# Revit family: Overhead_Door-CHI-Skyline_Flush-LP
name_source: partatom
category: Specialty Equipment
units: mm (PartAtom-declared; Revit-internal decimal feet)

## family parameters
Always vertical = Yes
Cut with Voids When Loaded = No
Host = Wall
OmniClass Number = 23.30.10.21
OmniClass Title = Special Function Doors
Part Type = Normal
Room Calculation Point = No
Round Connector Dimension = Use Diameter
Shared = No

## types (57) — shared parameters
Assembly Code = B2050.10
C Door Bottom Offset = 0.03'
C OFG = 0.00'
C Panel Size = 2
C Side Rail Radius = 1.25'
Certified Windload = Yes
Construction Type = Glass garage doors
Default Elevation = 0.00'
Description = Skyline Garage Doors
Fire Rating = Contact Manufacturer for More Information
Glass Finish = Glass - C.H.I Overhead Doors - Frosted
Impact = Yes
Keynote = 08 30 00
Load Classification = Other
Long Panel = Yes
Manufacturer = C.H.I. Overhead Doors
Manufacturer Fax Number = 800-738-5006
Material Disclaimer = Accents Woodtones, when ordered, contain non-repeating patterns. Color discrepancies may appear differently on desktop displays. Contact Manufacturer for Availability of Finishes per Model
Number of Phases = 1
Number of Poles = 1
Product Documentation Link = https://www.chiohd.com
Product Page URL = https://www.chiohd.com
Short Panel = No
Thickness = 0.17'
URL = https://www.chiohd.com
Version = 2021-v1.a
Voltage = 115 V

## per-type parameters (varying)
| type | Air Infiltration | C Model | DASMA Thermal Verification Program | Flame Spread | IECC Compliant | Model | Panel Finish | R-Value | Steel Gauge | U Factor |
| 2147 - Almond | Contact Manufacturer for More Information | 5 | No | Contact Manufacturer for More Information | No | 2147 | Metal - Powder Coat - C.H.I Overhead Doors - Almond | 10.29 | 27 | 0.29 |
| 2147 - Black | Contact Manufacturer for More Information | 5 | No | Contact Manufacturer for More Information | No | 2147 | Metal - Powder Coat - C.H.I Overhead Doors - Black | 10.29 | 27 | 0.29 |
| 2147 - Brown | Contact Manufacturer for More Information | 5 | No | Contact Manufacturer for More Information | No | 2147 | Metal - Powder Coat - C.H.I Overhead Doors - Brown | 10.29 | 27 | 0.29 |
| 2147 - Graphite | Contact Manufacturer for More Information | 5 | No | Contact Manufacturer for More Information | No | 2147 | Metal - Powder Coat - C.H.I Overhead Doors - Graphite | 10.29 | 27 | 0.29 |
| 2147 - Gray | Contact Manufacturer for More Information | 5 | No | Contact Manufacturer for More Information | No | 2147 | Metal - Powder Coat - C.H.I Overhead Doors - Gray | 10.29 | 27 | 0.29 |
| 2147 - Sandstone | Contact Manufacturer for More Information | 5 | No | Contact Manufacturer for More Information | No | 2147 | Metal - Powder Coat - C.H.I Overhead Doors - Sandstone | 10.29 | 27 | 0.29 |
| 2147 - White | Contact Manufacturer for More Information | 5 | No | Contact Manufacturer for More Information | No | 2147 | Metal - Powder Coat - C.H.I Overhead Doors - White | 10.29 | 27 | 0.29 |
| 2147 - Carbon Oak | Contact Manufacturer for More Information | 5 | No | Contact Manufacturer for More Information | No | 2147 | Wood - Accents Woodtones - C.H.I Overhead Doors - Skyline Flush - Carbon Oak | 10.29 | 27 | 0.29 |
| 2147 - Cedar | Contact Manufacturer for More Information | 5 | No | Contact Manufacturer for More Information | No | 2147 | Wood - Accents Woodtones - C.H.I Overhead Doors - Skyline Flush - Cedar | 10.29 | 27 | 0.29 |
| 2147 - Dark Oak | Contact Manufacturer for More Information | 5 | No | Contact Manufacturer for More Information | No | 2147 | Wood - Accents Woodtones - C.H.I Overhead Doors - Skyline Flush - Dark Oak | 10.29 | 27 | 0.29 |
| 2147 - Driftwood | Contact Manufacturer for More Information | 5 | No | Contact Manufacturer for More Information | No | 2147 | Wood - Accents Woodtones - C.H.I Overhead Doors - Skyline Flush - Driftwood | 10.29 | 27 | 0.29 |
| 2147 - Mahogany | Contact Manufacturer for More Information | 5 | No | Contact Manufacturer for More Information | No | 2147 | Wood - Accents Woodtones - C.H.I Overhead Doors - Skyline Flush - Mahogany | 10.29 | 27 | 0.29 |
| 2147 - Natural Oak | Contact Manufacturer for More Information | 5 | No | Contact Manufacturer for More Information | No | 2147 | Wood - Accents Woodtones - C.H.I Overhead Doors - Skyline Flush - Natural Oak | 10.29 | 27 | 0.29 |
| 2147 - Walnut | Contact Manufacturer for More Information | 5 | No | Contact Manufacturer for More Information | No | 2147 | Wood - Accents Woodtones - C.H.I Overhead Doors - Skyline Flush - Walnut | 10.29 | 27 | 0.29 |
| 2148 - Almond | 0.1 | 6 | Yes | 15 | Yes | 2148 | Metal - Powder Coat - C.H.I Overhead Doors - Almond | 17.54 | 27 | 0.19 |
| 2148 - Black | 0.1 | 6 | Yes | 15 | Yes | 2148 | Metal - Powder Coat - C.H.I Overhead Doors - Black | 17.54 | 27 | 0.19 |
| 2148 - Bronze | 0.1 | 6 | Yes | 15 | Yes | 2148 | Metal - Powder Coat - C.H.I Overhead Doors - Bronze | 17.54 | 27 | 0.19 |
| 2148 - Brown | 0.1 | 6 | Yes | 15 | Yes | 2148 | Metal - Powder Coat - C.H.I Overhead Doors - Brown | 17.54 | 27 | 0.19 |
| 2148 - Desert Tan | 0.1 | 6 | Yes | 15 | Yes | 2148 | Metal - Powder Coat - C.H.I Overhead Doors - Desert Tan | 17.54 | 27 | 0.19 |
| 2148 - Graphite | 0.1 | 6 | Yes | 15 | Yes | 2148 | Metal - Powder Coat - C.H.I Overhead Doors - Graphite | 17.54 | 27 | 0.19 |
| 2148 - Gray | 0.1 | 6 | Yes | 15 | Yes | 2148 | Metal - Powder Coat - C.H.I Overhead Doors - Gray | 17.54 | 27 | 0.19 |
| 2148 - Sandstone | 0.1 | 6 | Yes | 15 | Yes | 2148 | Metal - Powder Coat - C.H.I Overhead Doors - Sandstone | 17.54 | 27 | 0.19 |
| 2148 - White | 0.1 | 6 | Yes | 15 | Yes | 2148 | Metal - Powder Coat - C.H.I Overhead Doors - White | 17.54 | 27 | 0.19 |
| 2148 - Cedar | 0.1 | 6 | Yes | 15 | Yes | 2148 | Wood - Accents Woodtones - C.H.I Overhead Doors - Skyline Flush - Cedar | 17.54 | 27 | 0.19 |
| 2148 - Dark Oak | 0.1 | 6 | Yes | 15 | Yes | 2148 | Wood - Accents Woodtones - C.H.I Overhead Doors - Skyline Flush - Dark Oak | 17.54 | 27 | 0.19 |
| 2148 - Driftwood | 0.1 | 6 | Yes | 15 | Yes | 2148 | Wood - Accents Woodtones - C.H.I Overhead Doors - Skyline Flush - Driftwood | 17.54 | 27 | 0.19 |
| 2148 - Mahogany | 0.1 | 6 | Yes | 15 | Yes | 2148 | Wood - Accents Woodtones - C.H.I Overhead Doors - Skyline Flush - Mahogany | 17.54 | 27 | 0.19 |
| 2148 - Natural Oak | 0.1 | 6 | Yes | 15 | Yes | 2148 | Wood - Accents Woodtones - C.H.I Overhead Doors - Skyline Flush - Natural Oak | 17.54 | 27 | 0.19 |
| 2148 - Walnut | 0.1 | 6 | Yes | 15 | Yes | 2148 | Wood - Accents Woodtones - C.H.I Overhead Doors - Skyline Flush - Walnut | 17.54 | 27 | 0.19 |
| 4140 - Almond | Contact Manufacturer for More Information | 11 | No | Contact Manufacturer for More Information | No | 4140 | Metal - Powder Coat - C.H.I Overhead Doors - Almond | Contact Manufacturer for More Information | 24 | Contact Manufacturer for More Information |
| 4140 - Brown | Contact Manufacturer for More Information | 11 | No | Contact Manufacturer for More Information | No | 4140 | Metal - Powder Coat - C.H.I Overhead Doors - Brown | Contact Manufacturer for More Information | 24 | Contact Manufacturer for More Information |
| 4140 - Sandstone | Contact Manufacturer for More Information | 11 | No | Contact Manufacturer for More Information | No | 4140 | Metal - Powder Coat - C.H.I Overhead Doors - Sandstone | Contact Manufacturer for More Information | 24 | Contact Manufacturer for More Information |
| 4140 - White | Contact Manufacturer for More Information | 11 | No | Contact Manufacturer for More Information | No | 4140 | Metal - Powder Coat - C.H.I Overhead Doors - White | Contact Manufacturer for More Information | 24 | Contact Manufacturer for More Information |
| 4141 - Almond | Contact Manufacturer for More Information | 12 | No | Contact Manufacturer for More Information | No | 4141 | Metal - Powder Coat - C.H.I Overhead Doors - Almond | 7.94 | 24 | Contact Manufacturer for More Information |
| 4141 - Brown | Contact Manufacturer for More Information | 12 | No | Contact Manufacturer for More Information | No | 4141 | Metal - Powder Coat - C.H.I Overhead Doors - Brown | 7.94 | 24 | Contact Manufacturer for More Information |
| 4141 - Sandstone | Contact Manufacturer for More Information | 12 | No | Contact Manufacturer for More Information | No | 4141 | Metal - Powder Coat - C.H.I Overhead Doors - Sandstone | 7.94 | 24 | Contact Manufacturer for More Information |
| 4141 - White | Contact Manufacturer for More Information | 12 | No | Contact Manufacturer for More Information | No | 4141 | Metal - Powder Coat - C.H.I Overhead Doors - White | 7.94 | 24 | Contact Manufacturer for More Information |
| 4150 - Almond | Contact Manufacturer for More Information | 13 | No | Contact Manufacturer for More Information | No | 4150 | Metal - Powder Coat - C.H.I Overhead Doors - Almond | Contact Manufacturer for More Information | 25 | Contact Manufacturer for More Information |
| 4150 - Black | Contact Manufacturer for More Information | 13 | No | Contact Manufacturer for More Information | No | 4150 | Metal - Powder Coat - C.H.I Overhead Doors - Black | Contact Manufacturer for More Information | 25 | Contact Manufacturer for More Information |
| 4150 - Bronze | Contact Manufacturer for More Information | 13 | No | Contact Manufacturer for More Information | No | 4150 | Metal - Powder Coat - C.H.I Overhead Doors - Bronze | Contact Manufacturer for More Information | 25 | Contact Manufacturer for More Information |
| 4150 - Brown | Contact Manufacturer for More Information | 13 | No | Contact Manufacturer for More Information | No | 4150 | Metal - Powder Coat - C.H.I Overhead Doors - Brown | Contact Manufacturer for More Information | 25 | Contact Manufacturer for More Information |
| 4150 - Desert Tan | Contact Manufacturer for More Information | 13 | No | Contact Manufacturer for More Information | No | 4150 | Metal - Powder Coat - C.H.I Overhead Doors - Desert Tan | Contact Manufacturer for More Information | 25 | Contact Manufacturer for More Information |
| 4150 - Gray | Contact Manufacturer for More Information | 13 | No | Contact Manufacturer for More Information | No | 4150 | Metal - Powder Coat - C.H.I Overhead Doors - Gray | Contact Manufacturer for More Information | 25 | Contact Manufacturer for More Information |
| 4150 - Sandstone | Contact Manufacturer for More Information | 13 | No | Contact Manufacturer for More Information | No | 4150 | Metal - Powder Coat - C.H.I Overhead Doors - Sandstone | Contact Manufacturer for More Information | 25 | Contact Manufacturer for More Information |
| 4150 - White | Contact Manufacturer for More Information | 13 | No | Contact Manufacturer for More Information | No | 4150 | Metal - Powder Coat - C.H.I Overhead Doors - White | Contact Manufacturer for More Information | 25 | Contact Manufacturer for More Information |
| 4150 - Classic Woodgrain | Contact Manufacturer for More Information | 13 | No | Contact Manufacturer for More Information | No | 4150 | Wood - Painted Woodtones - C.H.I Overhead Doors - Classic Woodgrain | Contact Manufacturer for More Information | 25 | Contact Manufacturer for More Information |
| 4150 - Modern Woodgrain | Contact Manufacturer for More Information | 13 | No | Contact Manufacturer for More Information | No | 4150 | Wood - Painted Woodtones - C.H.I Overhead Doors - Modern Woodgrain | Contact Manufacturer for More Information | 25 | Contact Manufacturer for More Information |
| 4151 - Almond | Contact Manufacturer for More Information | 14 | No | Contact Manufacturer for More Information | No | 4151 | Metal - Powder Coat - C.H.I Overhead Doors - Almond | 7.94 | 25 | Contact Manufacturer for More Information |
| 4151 - Black | Contact Manufacturer for More Information | 14 | No | Contact Manufacturer for More Information | No | 4151 | Metal - Powder Coat - C.H.I Overhead Doors - Black | 7.94 | 25 | Contact Manufacturer for More Information |
| 4151 - Bronze | Contact Manufacturer for More Information | 14 | No | Contact Manufacturer for More Information | No | 4151 | Metal - Powder Coat - C.H.I Overhead Doors - Bronze | 7.94 | 25 | Contact Manufacturer for More Information |
| 4151 - Brown | Contact Manufacturer for More Information | 14 | No | Contact Manufacturer for More Information | No | 4151 | Metal - Powder Coat - C.H.I Overhead Doors - Brown | 7.94 | 25 | Contact Manufacturer for More Information |
| 4151 - Desert Tan | Contact Manufacturer for More Information | 14 | No | Contact Manufacturer for More Information | No | 4151 | Metal - Powder Coat - C.H.I Overhead Doors - Desert Tan | 7.94 | 25 | Contact Manufacturer for More Information |
| 4151 - Gray | Contact Manufacturer for More Information | 14 | No | Contact Manufacturer for More Information | No | 4151 | Metal - Powder Coat - C.H.I Overhead Doors - Gray | 7.94 | 25 | Contact Manufacturer for More Information |
| 4151 - Sandstone | Contact Manufacturer for More Information | 14 | No | Contact Manufacturer for More Information | No | 4151 | Metal - Powder Coat - C.H.I Overhead Doors - Sandstone | 7.94 | 25 | Contact Manufacturer for More Information |
| 4151 - White | Contact Manufacturer for More Information | 14 | No | Contact Manufacturer for More Information | No | 4151 | Metal - Powder Coat - C.H.I Overhead Doors - White | 7.94 | 25 | Contact Manufacturer for More Information |
| 4151 - Classic Woodgrain | Contact Manufacturer for More Information | 14 | No | Contact Manufacturer for More Information | No | 4151 | Wood - Painted Woodtones - C.H.I Overhead Doors - Classic Woodgrain | 7.94 | 25 | Contact Manufacturer for More Information |
| 4151 - Modern Woodgrain | Contact Manufacturer for More Information | 14 | No | Contact Manufacturer for More Information | No | 4151 | Wood - Painted Woodtones - C.H.I Overhead Doors - Modern Woodgrain | 7.94 | 25 | Contact Manufacturer for More Information |

## geometry (parser evidence)
native form markers: Sweep x40
no freeform markers — native parametric forms only
